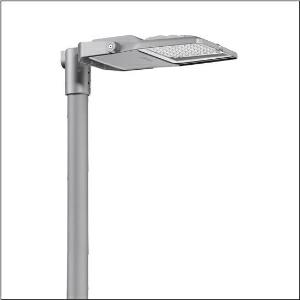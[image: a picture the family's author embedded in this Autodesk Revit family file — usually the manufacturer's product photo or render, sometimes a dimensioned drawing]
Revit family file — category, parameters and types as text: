
# Revit family: floodlight_fl_21_iq_mini___pl61_5xa7772d4c3a_23c5
name_source: partatom
category: Lighting Fixtures
units: mm (PartAtom-declared; Revit-internal decimal feet)

## family parameters
Cut with Voids When Loaded = No
Host = Face
Light Source = No
Part Type = Normal
Room Calculation Point = No
Round Connector Dimension = Use Diameter
Shared = No

## types (1)
- --- (1 x LED, 18260 lm, 143 W, 4000K)
    Apparent Load = 143 VA
    CIE Flux Codes = 33 65 98 100 100
    Color Rendering = 70
    Color Temperature = 4000K
    Default Elevation = 1800 mm
    Description = Floodlight FL 21 iQ mini, floodlight, primary light control with lens, of PMMA, primary optical cover: protective disc, of toughened safety glass, transparent, light distribution: PL61, light emission: direct distribution, installation type: surface-mounted, LED, High Power LED, rated luminous flux: 18.260lm, luminous efficacy: 128lm/W, light colour: 740, colour temperature: 4000K, control: Auto-Match, Temp-Guard, Night-Set, Smart-Wire, Desk-Remote (wireless, voltage-free reading and setting of iQ features in the workshop via application-optimized NFC function/RFID function), optimised constant luminous flux control (CLO 2.0), Light-Fading, Lumen-Switch, with terminal, 6-pole, mains connection: 220..240V, AC, 50/60Hz, start of lifetime: 143W, end of service life: 152W, reduction: 61W, luminaire housing, of diecast aluminium, powder-coated, Siteco® metallic grey (DB 702S), corrosivity category C5 mid according to DIN EN ISO 12944, sealing non-destructively replaceable, please order mast flange separately, mast bracket, of steel, galvanised, powder-coated, protection rating (complete): IP66, insulation class (complete): insulation class II (safety insulation), certification: CE, ENEC, VDE, protection symbol: D, impact resistance: IK08, permissible operating ambient temperature: -40..+40°C, permissible operating ambient temperature for outdoor applications: -40..+50°C, standard: DIN EN 12944, LABS conformity tested according to VDMA 24364:2018-05, packaging unit: 1 piece

Light Distribution: PL61
    Height = 70 mm
    Lamp = 1 x LED
    Lamp Light Flux = 18260 lm
    Lamp Power = 143 W
    Lamp count = 1
    Length = 485 mm
    Luminous efficacy = 128 lm/W
    Manufacturer = Siteco
    ModVariant = No
    Model = 5XA7772D4C3A
    Number of Poles = 1
    OnlyDefault = Yes
    Power Factor = 1
    Product Name = Floodlight FL 21 iQ mini | PL61
    Product group = floodlight | pylon annexe
    ProductGroupID = 6200
    Protection Class = Protection class II
    Protection Degree = IP 66
    RLX_Detail_Level = 1
    RLX_Emergency_Light_Flux = 0 lm
    RLX_Emergency_Type = 0
    RLX_Emergency_Type_DB = No
    RlxData = <blob elided: 101489 chars, md5=c8588c81>
    Socket = socket
    Standby Power = 0 W
    System Light Flux = 18260 lm
    System Power = 143 W
    Type Comments = factory setting: luminous flux: 100 % | dim-lin: 254 | 730 mA
    Type Image = l_1007125.jpg
    URL = http://relux.com
    VarID = @adj_143409
    Voltage = 0 V
    Weight = 0.00 kg
    Width = 337 mm

## geometry (parser evidence)
native form markers: Blend x4, Sweep x12
no freeform markers — native parametric forms only
